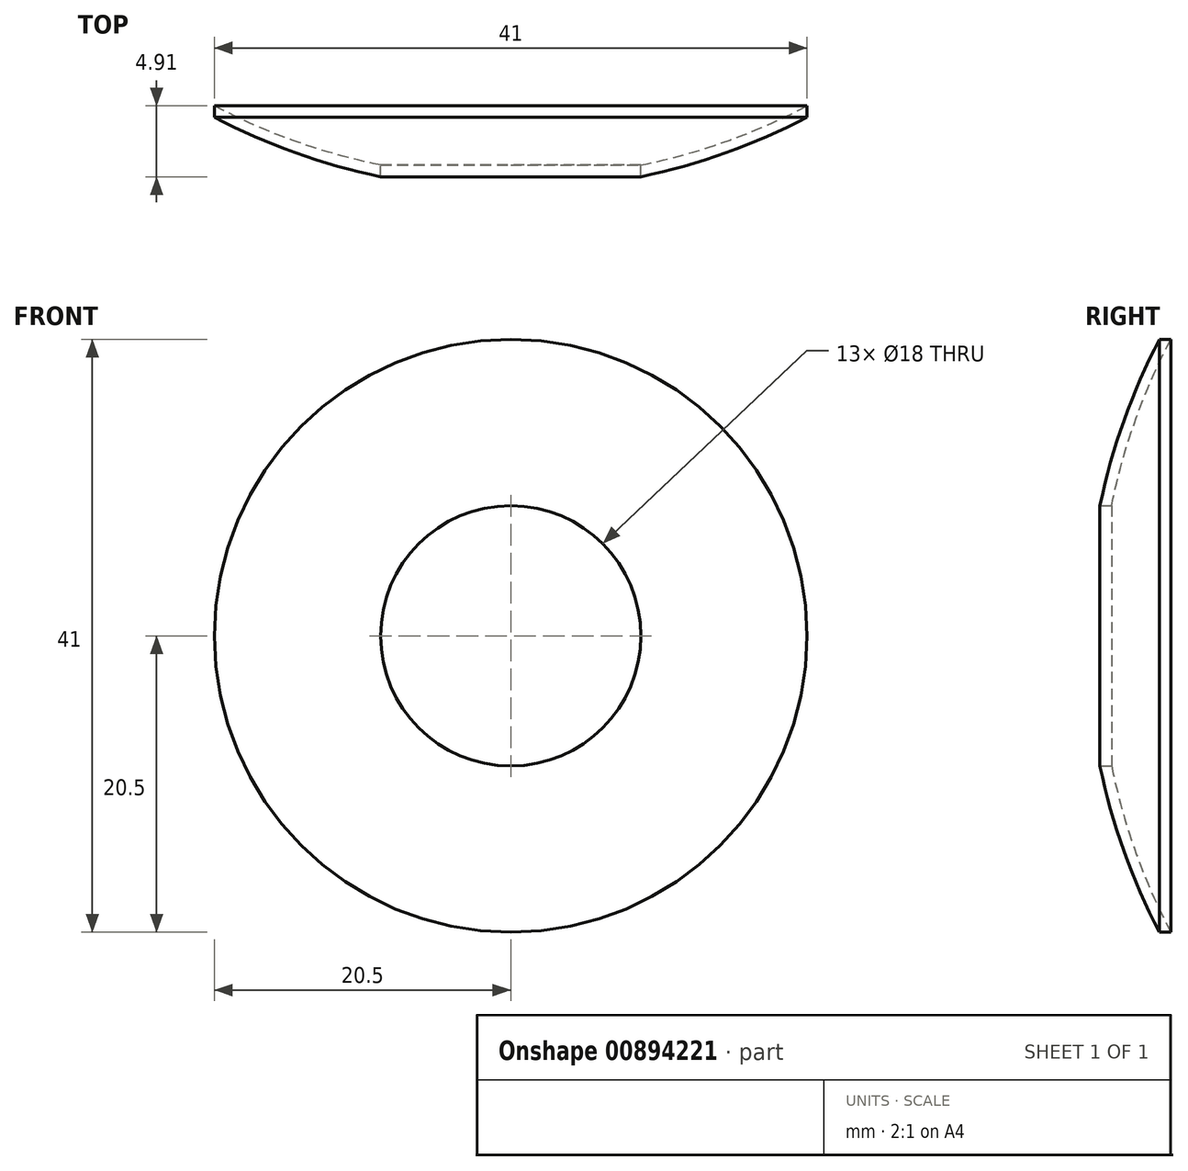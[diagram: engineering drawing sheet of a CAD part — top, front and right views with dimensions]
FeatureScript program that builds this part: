
annotation { "Feature Type Name" : "Feature", "Feature Type Description" : "" }
export const myFeature = defineFeature(function(context is Context, id is Id, definition is map)
    precondition{}
    {
        {
            var Q0;
            Q0=qCreatedBy(makeId("Right.planeOp"),FACE);
            var sketch = newSketch(context, id + "F0", { "sketchPlane" : qUnion([Q0])});
            skLineSegment(sketch, "E0", {"start": v(-43.38, 9) * mm, "end": v(-42.58, 9) * mm});
            skArc(sketch, "E1", {"start": v(-39.27, 20.5) * mm, "mid": v(-41.72, 14.9) * mm, "end": v(-43.38, 9) * mm});
            skLineSegment(sketch, "E2", {"start": v(-39.27, 20.5) * mm, "end": v(-38.47, 20.5) * mm});
            skArc(sketch, "E3", {"start": v(-38.47, 20.5) * mm, "mid": v(-40.93, 14.9) * mm, "end": v(-42.58, 9) * mm});
            skLineSegment(sketch, "E4", {"start": v(0, 0) * mm, "end": v(-43.38, 0) * mm});
            skSolve(sketch);
        }
        {
            var Q0;
            Q0=makeQuery(id+"F0.imprint","IMPRINT",FACE,{"disambiguationData":[TD([[makeQuery(id+"F0.imprint","IMPRINT",EDGE,{"derivedFrom":sQuery(id+"F0.wireOp",EDGE,"E0")}),1.0]])]});
            var Q1;
            Q1=sQuery(id+"F0.wireOp",EDGE,"E4");
            revolve(context, id + "F1", {"surfaceOperationType" : NewSurfaceOperationType.NEW, "entities" : qUnion([Q0]), "axis" : qUnion([Q1]), "revolveType" : RevolveType.FULL});
        }
    });
